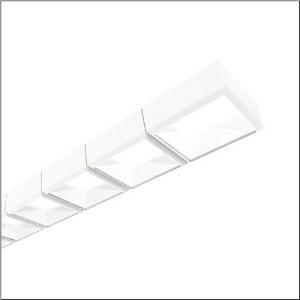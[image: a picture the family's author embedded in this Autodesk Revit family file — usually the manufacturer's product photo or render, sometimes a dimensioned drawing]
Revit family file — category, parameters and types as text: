
# Revit family: scriptus_r__11_5mz212d04wa_64be
name_source: partatom
category: Lighting Fixtures
units: mm (PartAtom-declared; Revit-internal decimal feet)

## family parameters
Cut with Voids When Loaded = No
Host = Face
Light Source = No
Part Type = Normal
Room Calculation Point = No
Round Connector Dimension = Use Diameter
Shared = No

## types (1)
- Scriptus® 11 (1 x LED 4000K / CRI = 80 (unbekannt), 2410 lm, 4000K)
    Apparent Load = 35 VA
    CIE Flux Codes = 82 95 99 100 100
    Color Rendering = 80
    Color Temperature = 4000K
    Default Elevation = 1800 mm
    Description = Scriptus® 11, office luminaire, primary optical cover: lenses, CAT 2 (L<= 3000cd/m²), light emission: direct distribution, primary light characteristic: symmetric, installation type: surface-mounted, LED, rated luminous flux: 4.810lm, luminous efficacy: 139lm/W, light colour: 840, colour temperature: 4000K, control gear: DALI, with terminal, 5-pole, mains connection: 230V, AC, 50Hz, rated input power: 35W, housing, luminaire housing, of aluminium, traffic white (RAL 9016), length: 1.658mm, width: 114mm, height: 57mm, protection rating (complete): IP20, insulation class (complete): insulation class I (protective earthing), certification: CE, ENEC, VDE, protection symbol: F, permissible operating ambient temperature: 0..+35°C, standard: EN 50419, packaging unit: 1 piece
    Height = 57 mm
    Lamp = 1 x LED 4000K / CRI >= 80 (unbekannt)
    Lamp Light Flux = 2410 lm
    Lamp count = 1
    Length = 1658 mm
    Luminous efficacy = 139 lm/W
    Manufacturer = Siteco
    ModVariant = No
    Model = 5MZ212D04WA
    Mounting Place = Ceiling
    Mounting Type = Surface mounted
    Number of Poles = 1
    OnlyDefault = Yes
    Power Factor = 1
    Product Name = Scriptus® 11
    Product group = office luminaire | ceiling mounted
    ProductGroupID = 303
    Protection Class = Protection class I
    Protection Degree = IP 20
    RLX_Detail_Level = 1
    RLX_Emergency_Light_Flux = 0 lm
    RLX_Emergency_Type = 0
    RLX_Emergency_Type_DB = No
    RlxData = <blob elided: 29485 chars, md5=e48b72fb>
    Socket = socket
    Standby Power = 0 W
    System Light Flux = 4820 lm
    System Power = 35 W
    Type Comments = Product without accessories
    Type Image = l_1004833.jpg
    URL = http://relux.com
    VarID = ---
    Voltage = 0 V
    Weight = 0.00 kg
    Width = 114 mm

## geometry (parser evidence)
native form markers: Blend x4, Sweep x17
no freeform markers — native parametric forms only
